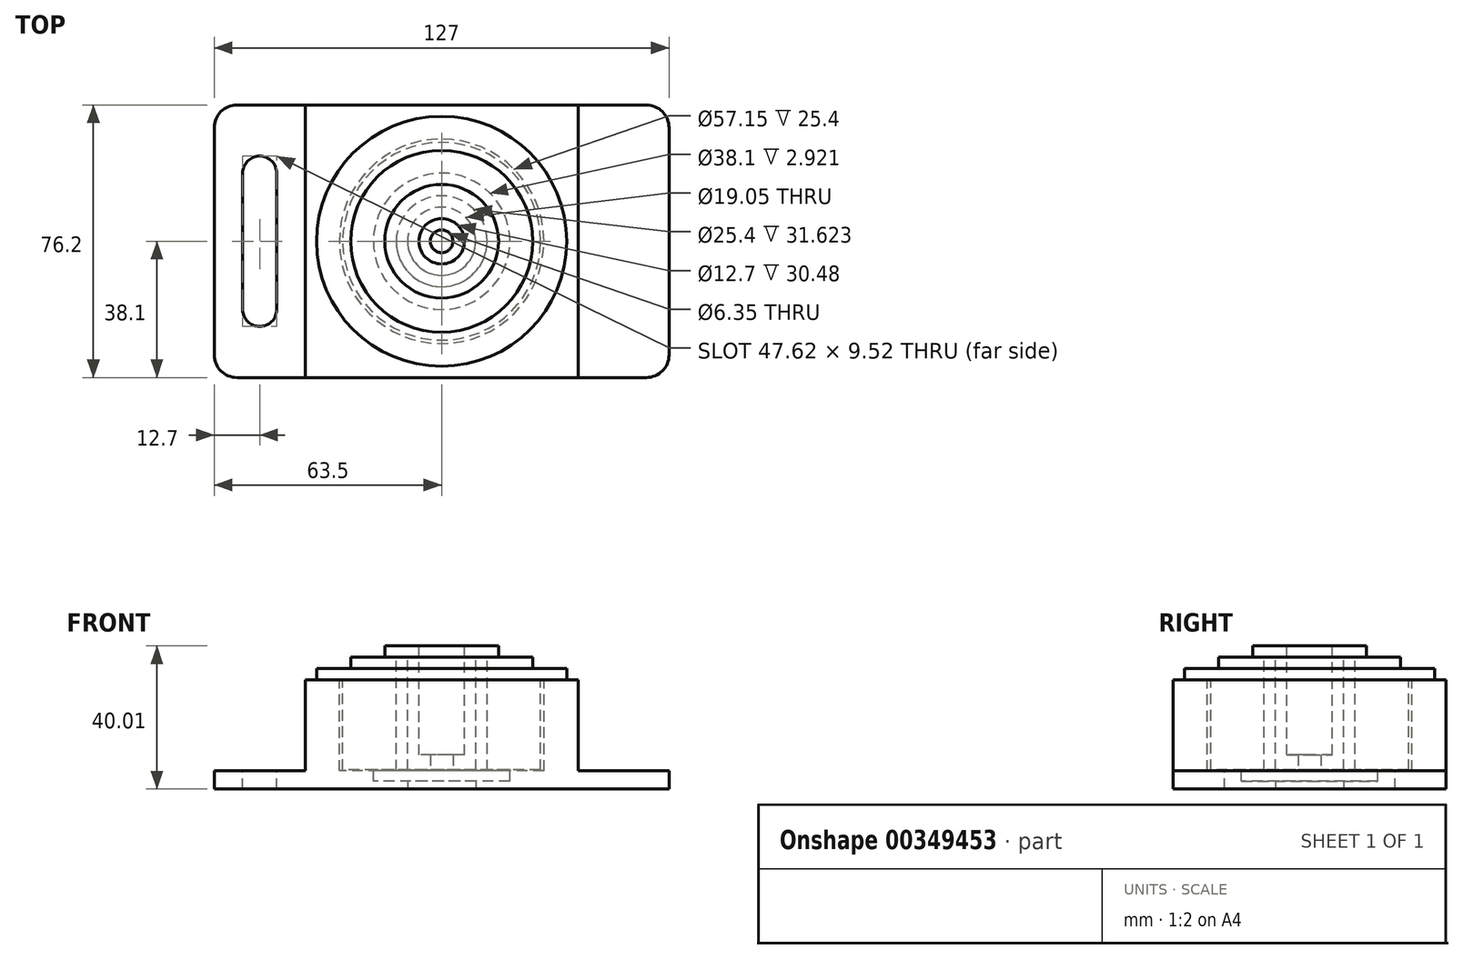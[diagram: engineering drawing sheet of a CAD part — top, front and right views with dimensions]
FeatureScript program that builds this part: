
annotation { "Feature Type Name" : "Feature", "Feature Type Description" : "" }
export const myFeature = defineFeature(function(context is Context, id is Id, definition is map)
    precondition{}
    {
        {
            var Q0;
            Q0=qCreatedBy(makeId("Top.planeOp"),FACE);
            var sketch = newSketch(context, id + "F0", { "sketchPlane" : qUnion([Q0])});
            skLineSegment(sketch, "E0.bottom", {"start": v(63.5, -38.1) * mm, "end": v(-63.5, -38.1) * mm});
            skLineSegment(sketch, "E0.top", {"start": v(63.5, 38.1) * mm, "end": v(-63.5, 38.1) * mm});
            skLineSegment(sketch, "E0.left", {"start": v(63.5, -38.1) * mm, "end": v(63.5, 38.1) * mm});
            skLineSegment(sketch, "E0.right", {"start": v(-63.5, -38.1) * mm, "end": v(-63.5, 38.1) * mm});
            skPoint(sketch, "E0.middle", {"position": v(0, 0) * mm});
            skSolve(sketch);
        }
        {
            var Q0;
            Q0=makeQuery(id+"F0.imprint","IMPRINT",FACE,{"disambiguationData":[TD([[makeQuery(id+"F0.imprint","IMPRINT",EDGE,{"derivedFrom":sQuery(id+"F0.wireOp",EDGE,"E0.bottom")}),-1.0]])]});
            extrude(context, id + "F1", {"entities" : qUnion([Q0]), "depth" : 5.08 * mm});
        }
        {
            var Q0;
            Q0=makeQuery(id+"F1.opExtrude","CAP_FACE",FACE,{"disambiguationData":[OSD([sQuery(id+"F0.wireOp",EDGE,"E0.bottom"),sQuery(id+"F0.wireOp",EDGE,"E0.top"),sQuery(id+"F0.wireOp",EDGE,"E0.left"),sQuery(id+"F0.wireOp",EDGE,"E0.right")])],"isStart":false});
            var sketch = newSketch(context, id + "F2", { "sketchPlane" : qUnion([Q0])});
            skLineSegment(sketch, "E1.bottom", {"start": v(38.1, -38.1) * mm, "end": v(-38.1, -38.1) * mm});
            skLineSegment(sketch, "E1.top", {"start": v(38.1, 38.1) * mm, "end": v(-38.1, 38.1) * mm});
            skLineSegment(sketch, "E1.left", {"start": v(38.1, -38.1) * mm, "end": v(38.1, 38.1) * mm});
            skLineSegment(sketch, "E1.right", {"start": v(-38.1, -38.1) * mm, "end": v(-38.1, 38.1) * mm});
            skPoint(sketch, "E1.middle", {"position": v(0, 0) * mm});
            skSolve(sketch);
        }
        {
            var Q0;
            Q0 = qSketchRegion(id + "F2", true);
            extrude(context, id + "F3", {"entities" : qUnion([Q0]), "operationType" : NewBodyOperationType.ADD, "depth" : 25.4 * mm});
        }
        {
            var Q0;
            Q0=makeQuery(id+"F3.opExtrude","CAP_FACE",FACE,{"disambiguationData":[OSD([sQuery(id+"F2.wireOp",EDGE,"E1.bottom"),sQuery(id+"F2.wireOp",EDGE,"E1.top"),sQuery(id+"F2.wireOp",EDGE,"E1.left"),sQuery(id+"F2.wireOp",EDGE,"E1.right")])],"isStart":false});
            var sketch = newSketch(context, id + "F4", { "sketchPlane" : qUnion([Q0])});
            skCircle(sketch, "E2", {"center": v(0, 0) * mm, "radius": 28.58 * mm});
            skSolve(sketch);
        }
        {
            var Q0;
            Q0=makeQuery(id+"F4.imprint","IMPRINT",FACE,{"disambiguationData":[TD([[makeQuery(id+"F4.imprint","IMPRINT",EDGE,{"derivedFrom":sQuery(id+"F4.wireOp",EDGE,"E2")}),1.0]])]});
            extrude(context, id + "F5", {"entities" : qUnion([Q0]), "operationType" : NewBodyOperationType.REMOVE, "oppositeDirection" : true, "depth" : 25.4 * mm});
        }
        {
            var Q0;
            Q0=makeQuery(id+"F1.opExtrude","SWEPT_EDGE",EDGE,{"disambiguationData":[OSD([sQuery(id+"F0.wireOp",EDGE,"E0.bottom"),sQuery(id+"F0.wireOp",EDGE,"E0.left")])]});
            var Q1;
            Q1=makeQuery(id+"F1.opExtrude","SWEPT_EDGE",EDGE,{"disambiguationData":[OSD([sQuery(id+"F0.wireOp",EDGE,"E0.top"),sQuery(id+"F0.wireOp",EDGE,"E0.left")])]});
            var Q2;
            Q2=makeQuery(id+"F1.opExtrude","SWEPT_EDGE",EDGE,{"disambiguationData":[OSD([sQuery(id+"F0.wireOp",EDGE,"E0.top"),sQuery(id+"F0.wireOp",EDGE,"E0.right")])]});
            var Q3;
            Q3=makeQuery(id+"F1.opExtrude","SWEPT_EDGE",EDGE,{"disambiguationData":[OSD([sQuery(id+"F0.wireOp",EDGE,"E0.bottom"),sQuery(id+"F0.wireOp",EDGE,"E0.right")])]});
            fillet(context, id + "F6", {"entities" : qUnion([Q0, Q1, Q2, Q3]), "radius" : 6.35 * mm, "tangentPropagation" : true, "allowEdgeOverflow" : false});
        }
        {
            var Q0;
            {var subQ0=sQuery(id+"F0.wireOp",EDGE,"E0.top");var subQ1=sQuery(id+"F0.wireOp",EDGE,"E0.right");var subQ2=sQuery(id+"F0.wireOp",EDGE,"E0.bottom");Q0=makeQuery(id+"F3.boolean.opBoolean","SPLIT",FACE,{"disambiguationData":[TD([makeQuery(id+"F1.opExtrude","SWEPT_FACE",FACE,{"disambiguationData":[OSD([subQ1])]})])],"derivedFrom":makeQuery(id+"F1.opExtrude","CAP_FACE",FACE,{"disambiguationData":[OSD([subQ2,subQ0,sQuery(id+"F0.wireOp",EDGE,"E0.left"),subQ1])],"isStart":false})});}
            var sketch = newSketch(context, id + "F7", { "sketchPlane" : qUnion([Q0])});
            skArc(sketch, "E3", {"start": v(-46.04, 19.05) * mm, "mid": v(-50.8, 23.81) * mm, "end": v(-55.56, 19.05) * mm});
            skArc(sketch, "E4", {"start": v(-55.56, -19.05) * mm, "mid": v(-50.8, -23.81) * mm, "end": v(-46.04, -19.05) * mm});
            skLineSegment(sketch, "E5", {"start": v(-55.56, 19.05) * mm, "end": v(-55.56, -19.05) * mm});
            skLineSegment(sketch, "E6", {"start": v(-46.04, 19.05) * mm, "end": v(-46.04, -19.05) * mm});
            skSolve(sketch);
        }
        {
            var Q0;
            Q0=makeQuery(id+"F7.imprint","IMPRINT",FACE,{"disambiguationData":[TD([[makeQuery(id+"F7.imprint","IMPRINT",EDGE,{"derivedFrom":sQuery(id+"F7.wireOp",EDGE,"E3")}),1.0]])]});
            extrude(context, id + "F8", {"entities" : qUnion([Q0]), "operationType" : NewBodyOperationType.REMOVE, "oppositeDirection" : true, "depth" : 25.4 * mm});
        }
        {
            var Q0;
            Q0=makeQuery(id+"F4.imprint","IMPRINT",FACE,{"disambiguationData":[TD([[makeQuery(id+"F4.imprint","IMPRINT",EDGE,{"derivedFrom":sQuery(id+"F4.wireOp",EDGE,"E2")}),-1.0]])]});
            var sketch = newSketch(context, id + "F9", { "sketchPlane" : qUnion([Q0])});
            skCircle(sketch, "E7", {"center": v(0, 0) * mm, "radius": 34.93 * mm});
            skSolve(sketch);
        }
        {
            var Q0;
            Q0 = qSketchRegion(id + "F9", true);
            var Q1;
            Q1=sQuery(id+"F9.wireOp",EDGE,"E7");
            extrude(context, id + "F10", {"entities" : qUnion([Q0]), "surfaceEntities" : qUnion([Q1]), "depth" : 3.17 * mm});
        }
        {
            var Q0;
            Q0=makeQuery(id+"F4.imprint","IMPRINT",FACE,{"disambiguationData":[TD([[makeQuery(id+"F4.imprint","IMPRINT",EDGE,{"derivedFrom":sQuery(id+"F4.wireOp",EDGE,"E2")}),1.0]])]});
            var sketch = newSketch(context, id + "F11", { "sketchPlane" : qUnion([Q0])});
            skCircle(sketch, "E8", {"center": v(0, 0) * mm, "radius": 27.62 * mm});
            skSolve(sketch);
        }
        {
            var Q0;
            Q0 = qSketchRegion(id + "F11", true);
            extrude(context, id + "F12", {"entities" : qUnion([Q0]), "operationType" : NewBodyOperationType.ADD, "oppositeDirection" : true, "depth" : 25.15 * mm});
        }
        {
            var Q0;
            Q0=makeQuery(id+"F10.opExtrude","CAP_FACE",FACE,{"disambiguationData":[OSD([sQuery(id+"F9.wireOp",EDGE,"E7")])],"isStart":false});
            var sketch = newSketch(context, id + "F13", { "sketchPlane" : qUnion([Q0])});
            skCircle(sketch, "E9", {"center": v(0, 0) * mm, "radius": 19.05 * mm});
            skSolve(sketch);
        }
        {
            var Q0;
            Q0=makeQuery(id+"F13.imprint","IMPRINT",FACE,{"disambiguationData":[TD([[makeQuery(id+"F13.imprint","IMPRINT",EDGE,{"derivedFrom":sQuery(id+"F13.wireOp",EDGE,"E9")}),1.0]])]});
            extrude(context, id + "F14", {"entities" : qUnion([Q0]), "operationType" : NewBodyOperationType.REMOVE, "oppositeDirection" : true, "depth" : 31.5 * mm});
        }
        {
            var Q0;
            Q0=makeQuery(id+"F1.opExtrude","CAP_FACE",FACE,{"disambiguationData":[OSD([sQuery(id+"F0.wireOp",EDGE,"E0.bottom"),sQuery(id+"F0.wireOp",EDGE,"E0.top"),sQuery(id+"F0.wireOp",EDGE,"E0.left"),sQuery(id+"F0.wireOp",EDGE,"E0.right")])],"isStart":true});
            var sketch = newSketch(context, id + "F15", { "sketchPlane" : qUnion([Q0])});
            skCircle(sketch, "E10", {"center": v(0, 0) * mm, "radius": 9.53 * mm});
            skSolve(sketch);
        }
        {
            var Q0;
            Q0=makeQuery(id+"F15.imprint","IMPRINT",FACE,{"disambiguationData":[TD([[makeQuery(id+"F15.imprint","IMPRINT",EDGE,{"derivedFrom":sQuery(id+"F15.wireOp",EDGE,"E10")}),1.0]])]});
            extrude(context, id + "F16", {"entities" : qUnion([Q0]), "operationType" : NewBodyOperationType.REMOVE, "endBound" : BoundingType.UP_TO_NEXT, "oppositeDirection" : true, "depth" : 25.4 * mm});
        }
        {
            var Q0;
            Q0=makeQuery(id+"F10.opExtrude","CAP_FACE",FACE,{"disambiguationData":[OSD([sQuery(id+"F9.wireOp",EDGE,"E7")])],"isStart":false});
            var sketch = newSketch(context, id + "F17", { "sketchPlane" : qUnion([Q0])});
            skCircle(sketch, "E11", {"center": v(0, 0) * mm, "radius": 25.4 * mm});
            skSolve(sketch);
        }
        {
            var Q0;
            Q0 = qSketchRegion(id + "F17", true);
            var Q1;
            Q1=sQuery(id+"F17.wireOp",EDGE,"E11");
            extrude(context, id + "F18", {"entities" : qUnion([Q0]), "surfaceEntities" : qUnion([Q1]), "depth" : 3.17 * mm});
        }
        {
            var Q0;
            Q0=makeQuery(id+"F18.opExtrude","CAP_FACE",FACE,{"disambiguationData":[OSD([sQuery(id+"F17.wireOp",EDGE,"E11")])],"isStart":true});
            var sketch = newSketch(context, id + "F19", { "sketchPlane" : qUnion([Q0])});
            skCircle(sketch, "E12", {"center": v(0, 0) * mm, "radius": 19.05 * mm});
            skSolve(sketch);
        }
        {
            var Q0;
            Q0 = qSketchRegion(id + "F19", true);
            var Q1;
            Q1=sQuery(id+"F19.wireOp",EDGE,"E12");
            extrude(context, id + "F20", {"entities" : qUnion([Q0]), "operationType" : NewBodyOperationType.ADD, "surfaceEntities" : qUnion([Q1]), "depth" : 28.45 * mm});
        }
        {
            var Q0;
            Q0=makeQuery(id+"F18.opExtrude","CAP_FACE",FACE,{"disambiguationData":[OSD([sQuery(id+"F17.wireOp",EDGE,"E11")])],"isStart":false});
            var sketch = newSketch(context, id + "F21", { "sketchPlane" : qUnion([Q0])});
            skCircle(sketch, "E13", {"center": v(0, 0) * mm, "radius": 12.7 * mm});
            skSolve(sketch);
        }
        {
            var Q0;
            Q0=makeQuery(id+"F21.imprint","IMPRINT",FACE,{"disambiguationData":[TD([[makeQuery(id+"F21.imprint","IMPRINT",EDGE,{"derivedFrom":sQuery(id+"F21.wireOp",EDGE,"E13")}),1.0]])]});
            extrude(context, id + "F22", {"entities" : qUnion([Q0]), "operationType" : NewBodyOperationType.REMOVE, "endBound" : BoundingType.UP_TO_NEXT, "oppositeDirection" : true, "depth" : 25.4 * mm});
        }
        {
            var Q0;
            Q0=makeQuery(id+"F18.opExtrude","CAP_FACE",FACE,{"disambiguationData":[OSD([sQuery(id+"F17.wireOp",EDGE,"E11")])],"isStart":false});
            var sketch = newSketch(context, id + "F23", { "sketchPlane" : qUnion([Q0])});
            skCircle(sketch, "E14", {"center": v(0, 0) * mm, "radius": 15.87 * mm});
            skSolve(sketch);
        }
        {
            var Q0;
            Q0 = qSketchRegion(id + "F23", true);
            extrude(context, id + "F24", {"entities" : qUnion([Q0]), "depth" : 3.17 * mm});
        }
        {
            var Q0;
            Q0=makeQuery(id+"F24.opExtrude","CAP_FACE",FACE,{"disambiguationData":[OSD([sQuery(id+"F23.wireOp",EDGE,"E14")])],"isStart":true});
            var sketch = newSketch(context, id + "F25", { "sketchPlane" : qUnion([Q0])});
            skCircle(sketch, "E15", {"center": v(0, 0) * mm, "radius": 9.53 * mm});
            skSolve(sketch);
        }
        {
            var Q0;
            Q0 = qSketchRegion(id + "F25", true);
            extrude(context, id + "F26", {"entities" : qUnion([Q0]), "operationType" : NewBodyOperationType.ADD, "depth" : 31.5 * mm});
        }
        {
            var Q0;
            Q0=makeQuery(id+"F24.opExtrude","CAP_FACE",FACE,{"disambiguationData":[OSD([sQuery(id+"F23.wireOp",EDGE,"E14")])],"isStart":false});
            var sketch = newSketch(context, id + "F27", { "sketchPlane" : qUnion([Q0])});
            skCircle(sketch, "E16", {"center": v(0, 0) * mm, "radius": 6.35 * mm});
            skSolve(sketch);
        }
        {
            var Q0;
            Q0=makeQuery(id+"F27.imprint","IMPRINT",FACE,{"disambiguationData":[TD([[makeQuery(id+"F27.imprint","IMPRINT",EDGE,{"derivedFrom":sQuery(id+"F27.wireOp",EDGE,"E16")}),1.0]])]});
            var Q1;
            Q1=sQuery(id+"F27.wireOp",EDGE,"E16");
            extrude(context, id + "F28", {"entities" : qUnion([Q0]), "operationType" : NewBodyOperationType.REMOVE, "surfaceEntities" : qUnion([Q1]), "oppositeDirection" : true, "depth" : 30.48 * mm});
        }
        {
            var Q0;
            Q0=makeQuery(id+"F26.opExtrude","CAP_FACE",FACE,{"disambiguationData":[OSD([sQuery(id+"F25.wireOp",EDGE,"E15")])],"isStart":false});
            var sketch = newSketch(context, id + "F29", { "sketchPlane" : qUnion([Q0])});
            skCircle(sketch, "E17", {"center": v(0, 0) * mm, "radius": 3.18 * mm});
            skSolve(sketch);
        }
        {
            var Q0;
            Q0 = qSketchRegion(id + "F29", true);
            extrude(context, id + "F30", {"entities" : qUnion([Q0]), "operationType" : NewBodyOperationType.REMOVE, "oppositeDirection" : true, "depth" : 25.4 * mm});
        }
    });
